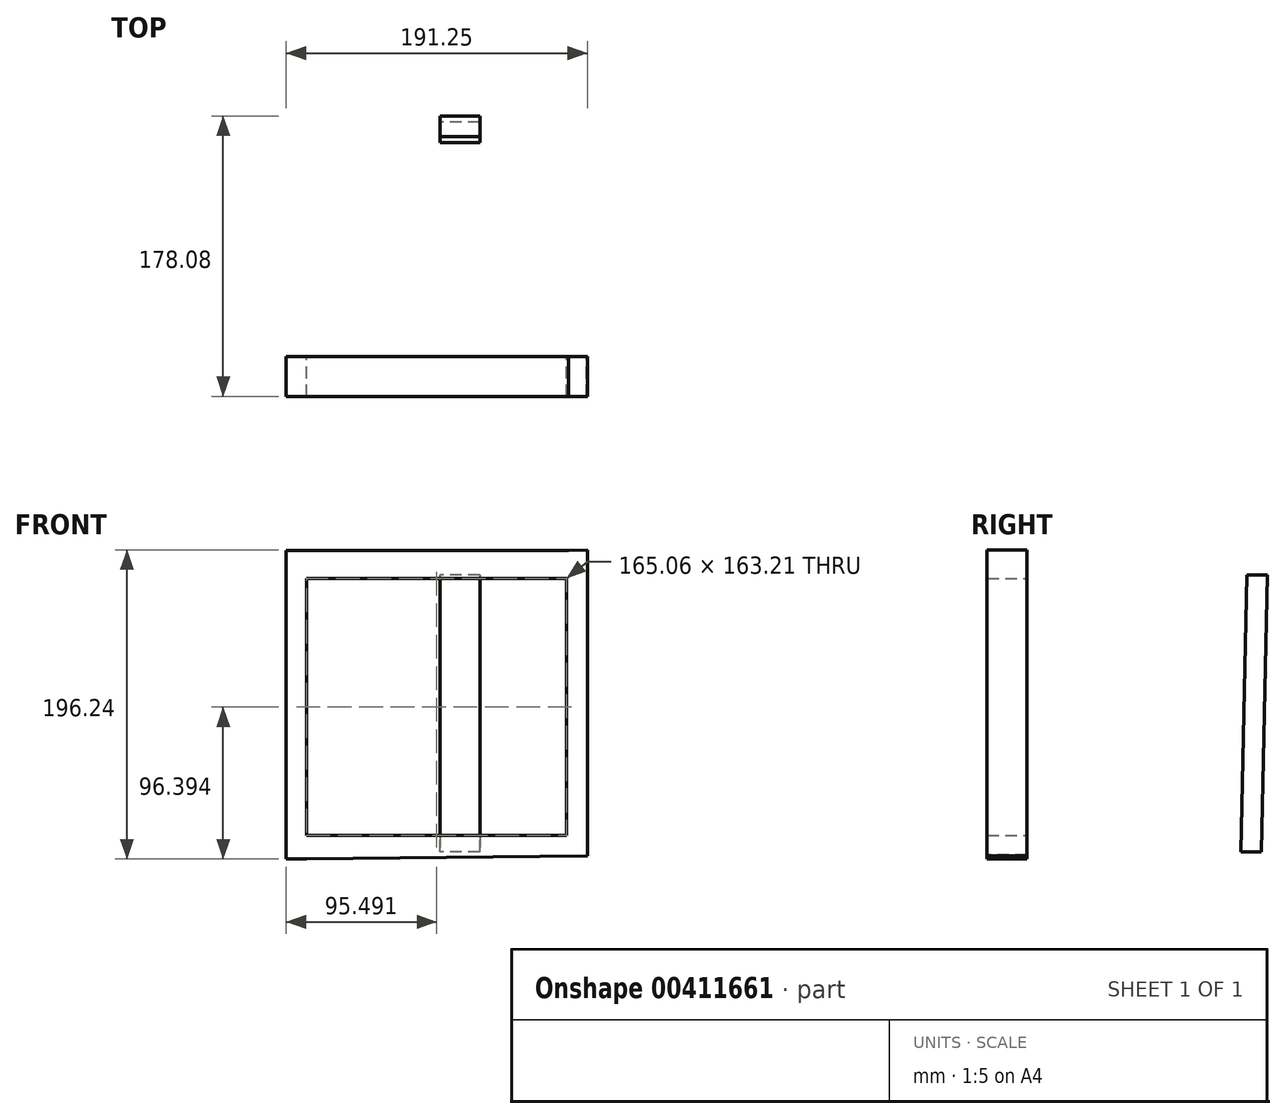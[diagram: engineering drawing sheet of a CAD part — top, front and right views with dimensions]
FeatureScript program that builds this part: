
annotation { "Feature Type Name" : "Feature", "Feature Type Description" : "" }
export const myFeature = defineFeature(function(context is Context, id is Id, definition is map)
    precondition{}
    {
        {
            var Q0;
            Q0=qCreatedBy(makeId("Front.planeOp"),FACE);
            var sketch = newSketch(context, id + "F0", { "sketchPlane" : qUnion([Q0])});
            skLineSegment(sketch, "E0", {"start": v(93.73, 97.28) * mm, "end": v(93.73, -97.1) * mm});
            skLineSegment(sketch, "E1", {"start": v(93.73, -97.1) * mm, "end": v(81.68, -97.1) * mm});
            skLineSegment(sketch, "E2", {"start": v(81.68, -97.1) * mm, "end": v(81.68, 96.83) * mm});
            skLineSegment(sketch, "E3", {"start": v(81.68, 96.83) * mm, "end": v(93.73, 97.28) * mm});
            skLineSegment(sketch, "E4", {"start": v(-97.52, 96.83) * mm, "end": v(81.68, 96.83) * mm});
            skLineSegment(sketch, "E5", {"start": v(81.68, 96.83) * mm, "end": v(-97.52, 96.83) * mm});
            skLineSegment(sketch, "E6", {"start": v(-97.52, 80.1) * mm, "end": v(81.68, 80.1) * mm});
            skLineSegment(sketch, "E7", {"start": v(-97.52, 96.83) * mm, "end": v(-97.52, 80.1) * mm});
            skLineSegment(sketch, "E8", {"start": v(-97.52, -96.42) * mm, "end": v(-97.52, 80.1) * mm});
            skLineSegment(sketch, "E9", {"start": v(-86.36, 80.1) * mm, "end": v(-86.36, -96.87) * mm});
            skLineSegment(sketch, "E10", {"start": v(-86.36, -96.87) * mm, "end": v(-97.52, -96.42) * mm});
            skLineSegment(sketch, "E11", {"start": v(81.68, -97.1) * mm, "end": v(-86.36, -96.87) * mm});
            skLineSegment(sketch, "E12", {"start": v(-86.36, -84.6) * mm, "end": v(81.68, -84.6) * mm});
            skSolve(sketch);
        }
        {
            var Q0;
            Q0 = qSketchRegion(id + "F0", true);
            extrude(context, id + "F1", {"entities" : qUnion([Q0]), "depth" : 25.4 * mm});
        }
        {
            var Q0;
            Q0=qCreatedBy(makeId("Front.planeOp"),FACE);
            var sketch = newSketch(context, id + "F2", { "sketchPlane" : qUnion([Q0])});
            skLineSegment(sketch, "E13", {"start": v(-97.5, 96.2) * mm, "end": v(-97.5, -98.96) * mm});
            skLineSegment(sketch, "E14", {"start": v(-97.5, -98.96) * mm, "end": v(-84.56, -98.96) * mm});
            skLineSegment(sketch, "E15", {"start": v(-84.56, -98.96) * mm, "end": v(-84.56, 96.47) * mm});
            skLineSegment(sketch, "E16", {"start": v(-84.56, 96.47) * mm, "end": v(-97.5, 96.2) * mm});
            skLineSegment(sketch, "E17", {"start": v(93.44, 96.47) * mm, "end": v(-84.56, 96.47) * mm});
            skLineSegment(sketch, "E18", {"start": v(-84.56, 79.04) * mm, "end": v(93.18, 79.04) * mm});
            skLineSegment(sketch, "E19", {"start": v(93.18, 79.04) * mm, "end": v(93.44, 96.47) * mm});
            skLineSegment(sketch, "E20", {"start": v(93.18, -97.1) * mm, "end": v(93.18, 79.04) * mm});
            skLineSegment(sketch, "E21", {"start": v(93.18, 79.04) * mm, "end": v(93.18, -97.1) * mm});
            skLineSegment(sketch, "E22", {"start": v(80.5, -96.58) * mm, "end": v(80.5, 79.04) * mm});
            skLineSegment(sketch, "E23", {"start": v(80.5, 79.04) * mm, "end": v(80.5, -96.58) * mm});
            skLineSegment(sketch, "E24", {"start": v(93.18, -97.1) * mm, "end": v(-84.56, -98.96) * mm});
            skLineSegment(sketch, "E25", {"start": v(-84.56, -98.96) * mm, "end": v(80.5, -96.58) * mm});
            skLineSegment(sketch, "E26", {"start": v(80.5, -96.58) * mm, "end": v(-84.56, -98.96) * mm});
            skLineSegment(sketch, "E27", {"start": v(-84.56, -84.17) * mm, "end": v(80.5, -84.17) * mm});
            skSolve(sketch);
        }
        {
            var Q0;
            Q0 = qSketchRegion(id + "F2", true);
            extrude(context, id + "F3", {"entities" : qUnion([Q0]), "operationType" : NewBodyOperationType.ADD, "depth" : 25.4 * mm});
        }
        {
            var Q0;
            Q0=qCreatedBy(makeId("Right.planeOp"),FACE);
            var sketch = newSketch(context, id + "F4", { "sketchPlane" : qUnion([Q0])});
            skLineSegment(sketch, "E28", {"start": v(0, 96.95) * mm, "end": v(152.68, 96.95) * mm});
            skLineSegment(sketch, "E29", {"start": v(152.68, 96.95) * mm, "end": v(152.68, 81.31) * mm});
            skLineSegment(sketch, "E30", {"start": v(152.68, 81.31) * mm, "end": v(0, 81.31) * mm});
            skLineSegment(sketch, "E31", {"start": v(0, 81.31) * mm, "end": v(152.68, 81.31) * mm});
            skLineSegment(sketch, "E32", {"start": v(13.06, -94.41) * mm, "end": v(0, -94.41) * mm});
            skLineSegment(sketch, "E33", {"start": v(0, -94.41) * mm, "end": v(148.85, -94.41) * mm});
            skLineSegment(sketch, "E34", {"start": v(148.85, -94.41) * mm, "end": v(152.68, 81.31) * mm});
            skLineSegment(sketch, "E35", {"start": v(139.69, 81.31) * mm, "end": v(135.86, -94.41) * mm});
            skLineSegment(sketch, "E36", {"start": v(135.86, -94.41) * mm, "end": v(136.18, -79.75) * mm});
            skLineSegment(sketch, "E37", {"start": v(136.18, -79.75) * mm, "end": v(0, -79.75) * mm});
            skSolve(sketch);
        }
        {
            var Q0;
            Q0 = qSketchRegion(id + "F4", true);
            extrude(context, id + "F5", {"entities" : qUnion([Q0]), "depth" : 25.4 * mm});
        }
    });
